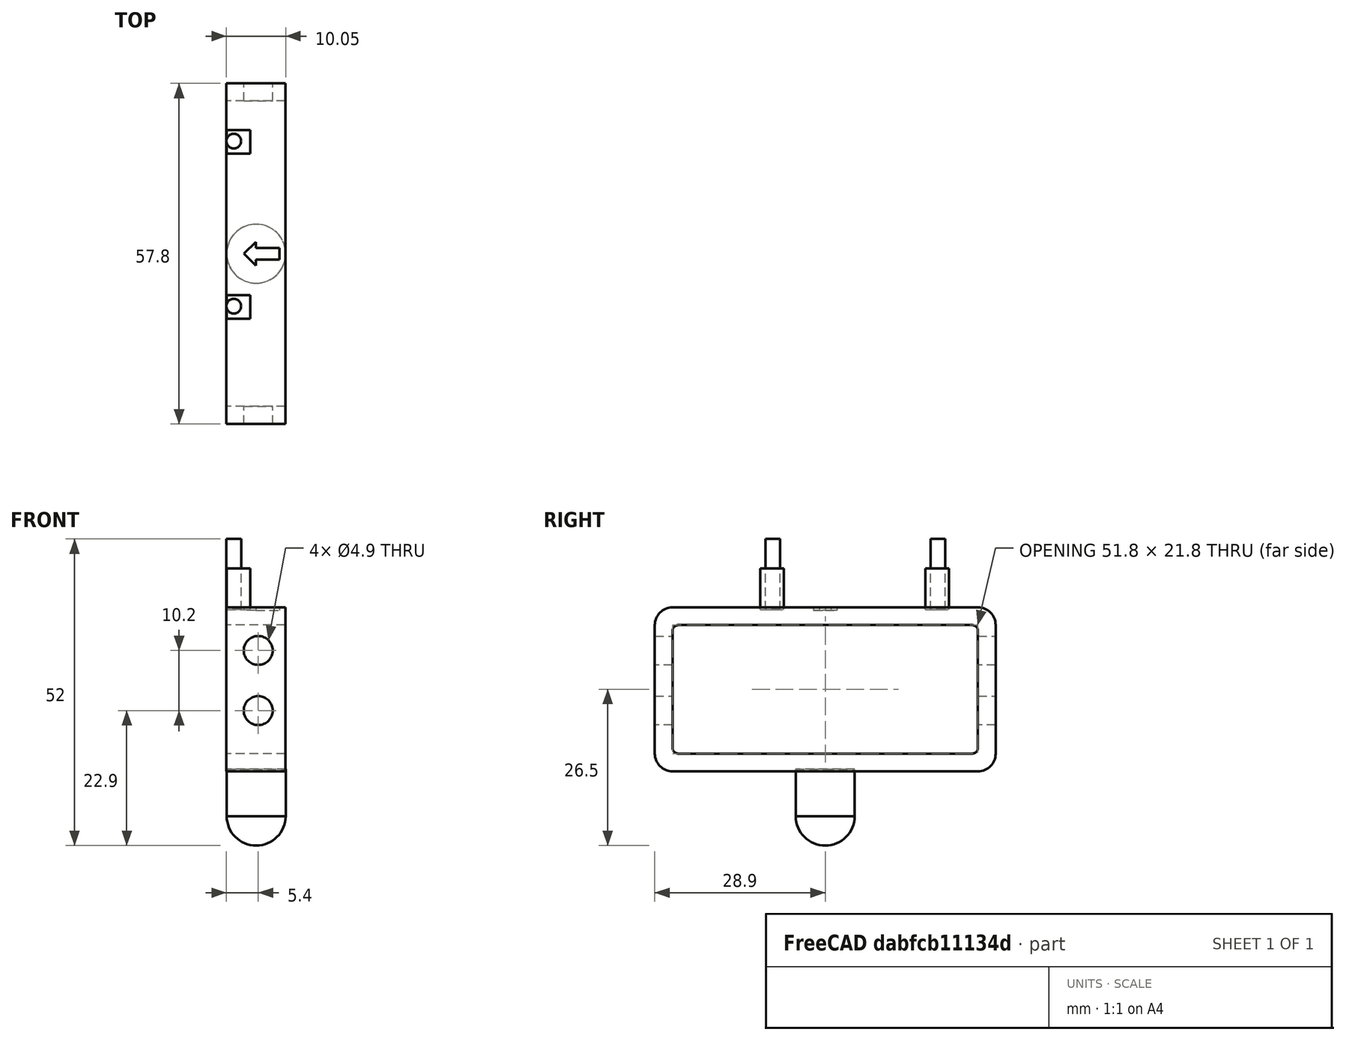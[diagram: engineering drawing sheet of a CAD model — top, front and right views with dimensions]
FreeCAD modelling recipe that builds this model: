
FCSTD DOCUMENT  (FreeCAD 0.17R13541 (Git))
Label: icelobot_f_V2
License: All rights reserved
LicenseURL: http://en.wikipedia.org/wiki/All_rights_reserved
objects: Part::Cylinder×3, Part::Box×3, Part::Feature×1, Part::Sphere×1, Part::Cut×1
note: 9 computed .brp shape members not serialized (recipe doc carries the construction recipe); baked Part::Feature solids carry a one-line shape summary decoded from their .brp

FEATURE [Part::Cylinder] Cylinder002  label="Cilindrof1"
  Angle = 360
  AttacherType = Attacher::AttachEngine3D
  Height = 12
  Placement = pos=(-39.8,-15.9,-33) rot=(0,0,1;0rad)
  Radius = 1.25
FEATURE [Part::Cylinder] Cylinder003  label="Cilindrof2"
  Angle = 360
  AttacherType = Attacher::AttachEngine3D
  Height = 12
  Placement = pos=(-39.8,-43.9,-33) rot=(0,0,1;0rad)
  Radius = 1.25
FEATURE [Part::Feature] Part__Feature001  label="front"
  Placement = pos=(-31.5,-35,-45) rot=(0.707107,0,-0.707107;3.14159rad)
  shape: bbox 10 x 57.8 x 27.8 mm, 30 faces (baked)
FEATURE [Part::Sphere] Sphere  label="Esfera"
  Angle1 = -90
  Angle2 = 90
  Angle3 = 360
  AttacherType = Attacher::AttachEngine3D
  Radius = 5
FEATURE [Part::Box] Box002  label="Cubo002"
  AttacherType = Attacher::AttachEngine3D
  Height = 10
  Length = 10
  Placement = pos=(-5,-5,0) rot=(0,0,1;0rad)
  Width = 10
FEATURE [Part::Cut] Cut
  Base = -> Sphere
  Placement = pos=(-36,-35,-68) rot=(0,0,1;0rad)
  Tool = -> Box002
FEATURE [Part::Cylinder] Cylinder004  label="Cilindro"
  Angle = 360
  AttacherType = Attacher::AttachEngine3D
  Height = 8
  Placement = pos=(-36,-35,-68) rot=(0,0,1;0rad)
  Radius = 5
FEATURE [Part::Box] Box003  label="Soprte Placa"
  AttacherType = Attacher::AttachEngine3D
  Height = 7
  Length = 4
  Placement = pos=(-41,-18,-33) rot=(0,0,1;0rad)
  Width = 4
FEATURE [Part::Box] Box004  label="Soprte Placa001"
  AttacherType = Attacher::AttachEngine3D
  Height = 7
  Length = 4
  Placement = pos=(-41,-46,-33) rot=(0,0,1;0rad)
  Width = 4
